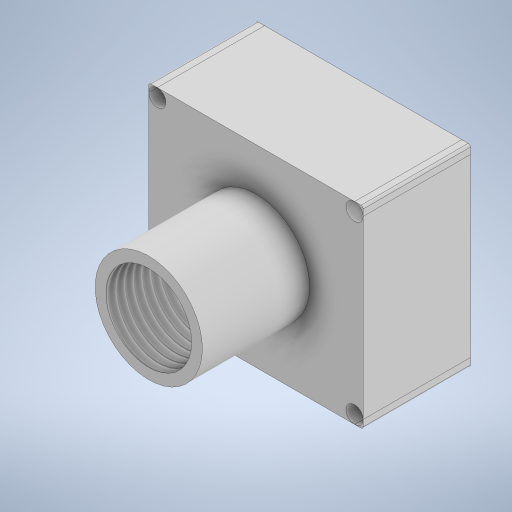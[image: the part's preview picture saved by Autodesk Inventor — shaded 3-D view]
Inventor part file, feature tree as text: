
AUTODESK INVENTOR PART (.ipt)
format: ipt  version: 2024 (Build 280153000, 153)  size: 304,128 bytes
history: native  units: in
note: dims shown in document units (in); Inventor stores cm internally (conversion verified against a paired STEP export)
features: extrude x3, sketch x3, fillet x2, thread x1
ambient origin geometry x8: Origin, YZ Plane, XZ Plane, XY Plane, X Axis, Y Axis, Z Axis, Center Point
bodies: Solid1 (feature_tree)
feature tree (9):
  extrude  "Extrusion1"  Depth=3.5433in
  extrude  "Extrusion2"  TaperAngle=0.0deg  [1 undecoded]
  extrude  "Extrusion3"  Depth=0.0394in TaperAngle=0.0deg
  thread  "Thread1"  [1 undecoded]
  fillet  "Fillet1"  Radius=0.0394in
  fillet  "Fillet2"  Radius=0.0394in
  sketch  "Sketch1"  dims[d0=3.937in d1=3.5433in]
  sketch  "Sketch2"  dims[d2=1.9685in d3=0.0in d8=0.0in d9=0.0in]
  sketch  "Sketch3"  dims[d12=1.9685in d13=0.0in d14=1.1811in d15=0.0in d16=0.0394in d17=0.0394in d10=0.0394in d11=0.0059in d18=0.0295in d19=0.0148in]
note: 2 required parameter values undecoded (feature->parameter linkage not recoverable at this tier; creation-order binding heuristic only, values carry confidence <= 0.55)
